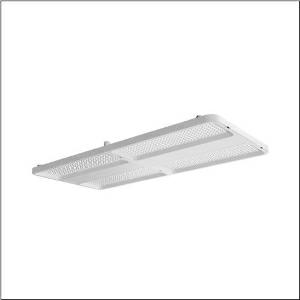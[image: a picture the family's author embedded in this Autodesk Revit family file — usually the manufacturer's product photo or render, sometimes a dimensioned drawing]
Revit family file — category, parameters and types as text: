
# Revit family: highbay_21_maxi_52hn12db4mda
name_source: partatom
category: Lighting Fixtures
units: mm (PartAtom-declared; Revit-internal decimal feet)

## family parameters
Cut with Voids When Loaded = No
Host = Face
Light Source = No
Part Type = Normal
Room Calculation Point = No
Round Connector Dimension = Use Diameter
Shared = No

## types (1)
- --- (1 x LED, 4230 lm, 22.6 W, 4000K)
    Apparent Load = 23 VA
    CIE Flux Codes = 90 98 100 100 100
    Color Rendering = 80
    Color Temperature = 4000K
    Default Elevation = 1800 mm
    Description = high bay luminaire Highbay 21 maxi; direct symmetric wide distribution, light control with lens of PMMA; UGR ≤ 22 (X = 4H | Y = 8H | S = 0.25H | reflection values 70/50/20); luminous flux: 28.000lm; light colour: 840, colour temperature: 4000K, MacAdam ≤ 3 SDCM (initial), colour rendering: CRI > 80; luminous efficacy: 194,4lm/W; rated service life: 75.000h (L80) at AT= ta max; control: DALI 2; luminaire connection: terminal, 5-pole, max. 2.5mm² (cable entry for one cable, Ø 8.5..16mm); mains connection: 230..240V, AC/DC 0/50..60Hz; connected load: 144W; protection rating (complete): IP66; insulation class (complete): insulation class I (protective earthing); protection symbol: D; impact resistance: IK08; certification: CE, ENEC, VDE, UKCA; luminaire for central battery installations according to EN 60598-2-22, internal wiring halogen-free; luminaire LABS conformity tested according to VDMA 24364:2018-05; Suitable for use in the food industry according to the specifications of IFS-Food, HACCP and/or BRC; housing frame of high-performance plastic PA6, matt traffic white (RAL 9016); cover of PMMA; dimension (LxWxH): 946 x 442 x 72mm; permissible operating ambient temperature: -40..+65°C (reducing of maximum allowable ambient temperature of 5°C with ceiling mounting); packaging unit: 1 piece; (delivery without accessories; please order mounting accessories separately)
    Height = 72 mm  [stored 0.23622 ft]
    Lamp = 1 x LED
    Lamp Light Flux = 4230 lm
    Lamp Power = 22.6 W
    Lamp count = 1
    Length = 946 mm
    Luminous efficacy = 187 lm/W
    Manufacturer = Siteco
    ModVariant = No
    Model = 52HN12DB4MDA
    Mounting Place = Ceiling
    Mounting Type = Pendant
    Number of Poles = 1
    OnlyDefault = Yes
    Power Factor = 1
    Product Name = Highbay 21 maxi
    Product group = high bay luminaire
    ProductGroupID = 902
    Protection Class = Protection class I
    Protection Degree = IP 66
    RLX_Detail_Level = 1
    RLX_Emergency_Light_Flux = 0 lm
    RLX_Emergency_Type = 0
    RLX_Emergency_Type_DB = No
    RlxData = <blob elided: 128273 chars, md5=e7572ebc>
    Socket = socket
    Standby Power = 0 W
    System Light Flux = 4230 lm
    System Power = 23 W
    Type Comments = : DC mode (central or group accumulator) initial emergency light level
    Type Image = l_1363244.jpg
    URL = http://relux.com
    VarID = @adj_017723
    Voltage = 0 V
    Weight = 0.00 kg
    Width = 442 mm

note: [stored X ft] marks values corroborated as IEEE doubles in the binary element streams (Revit-internal decimal feet)

## geometry (parser evidence)
native form markers: Blend x4, Sweep x9
no freeform markers — native parametric forms only
